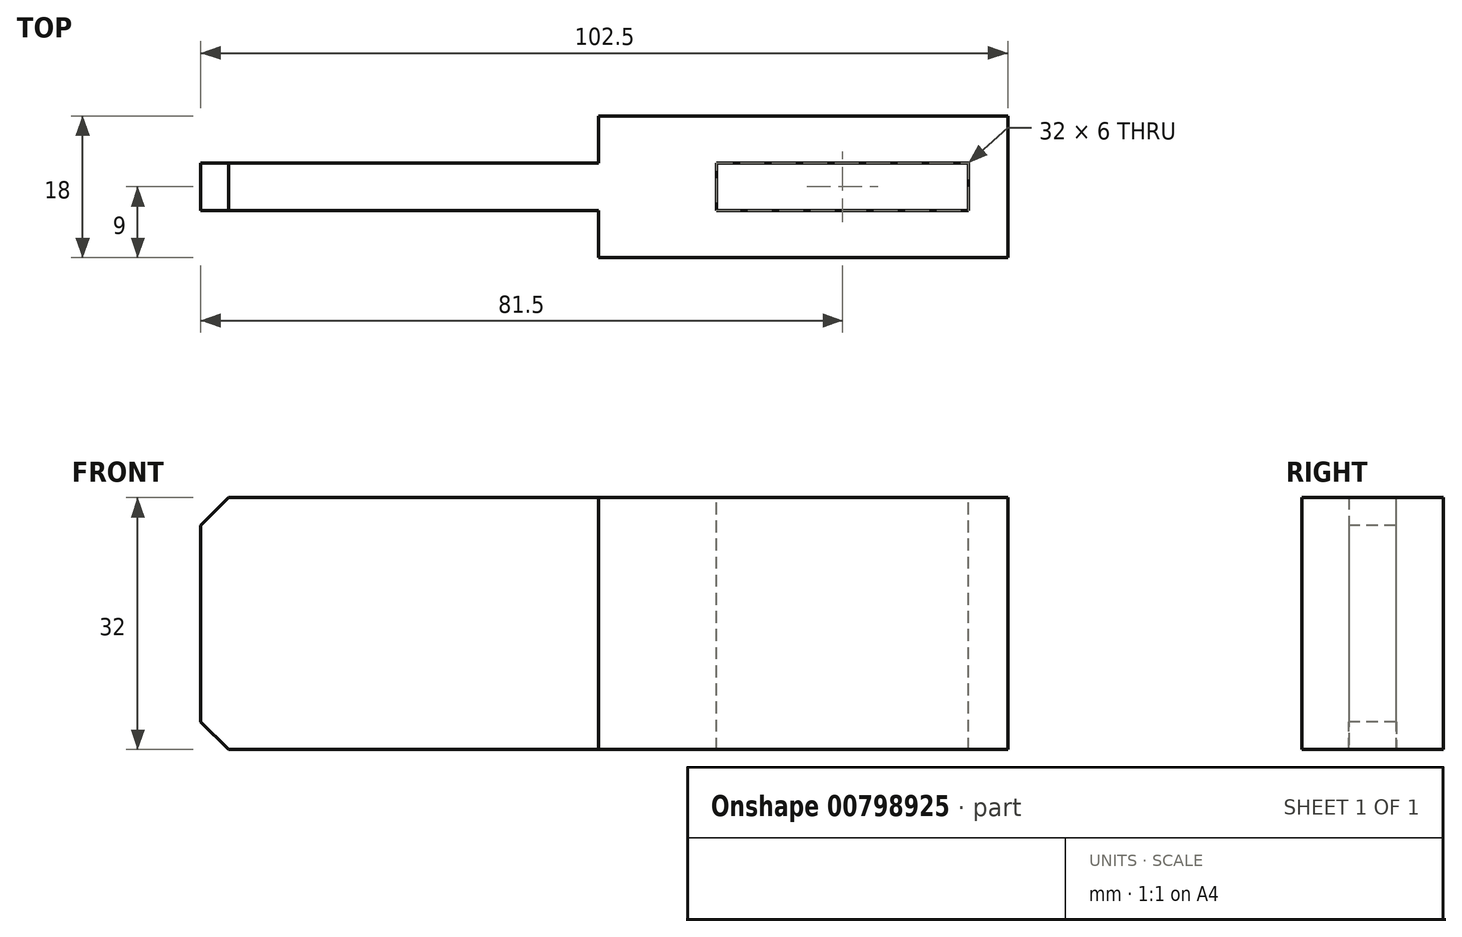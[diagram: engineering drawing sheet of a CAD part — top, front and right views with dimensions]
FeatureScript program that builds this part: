
annotation { "Feature Type Name" : "Feature", "Feature Type Description" : "" }
export const myFeature = defineFeature(function(context is Context, id is Id, definition is map)
    precondition{}
    {
        {
            var Q0;
            Q0=qCreatedBy(makeId("Front.planeOp"),FACE);
            var sketch = newSketch(context, id + "F0", { "sketchPlane" : qUnion([Q0])});
            skLineSegment(sketch, "E0", {"start": v(0, 0) * mm, "end": v(-52, 0) * mm});
            skLineSegment(sketch, "E1", {"start": v(-52, 0) * mm, "end": v(-52, 32) * mm});
            skLineSegment(sketch, "E2", {"start": v(-52, 32) * mm, "end": v(0, 32) * mm});
            skLineSegment(sketch, "E3", {"start": v(0, 32) * mm, "end": v(0, 0) * mm});
            skSolve(sketch);
        }
        {
            var Q0;
            Q0=makeQuery(id+"F0.imprint","IMPRINT",FACE,{"disambiguationData":[TD([[makeQuery(id+"F0.imprint","IMPRINT",EDGE,{"derivedFrom":sQuery(id+"F0.wireOp",EDGE,"E0")}),-1.0]])]});
            extrude(context, id + "F1", {"entities" : qUnion([Q0]), "endBound" : BoundingType.SYMMETRIC, "depth" : 18 * mm});
        }
        {
            var Q0;
            Q0=makeQuery(id+"F1.opExtrude","SWEPT_FACE",FACE,{"disambiguationData":[OSD([sQuery(id+"F0.wireOp",EDGE,"E2")])]});
            var sketch = newSketch(context, id + "F2", { "sketchPlane" : qUnion([Q0])});
            skLineSegment(sketch, "E4", {"start": v(0, 9) * mm, "end": v(0, 3) * mm});
            skLineSegment(sketch, "E5", {"start": v(0, 3) * mm, "end": v(-5, 3) * mm});
            skLineSegment(sketch, "E6", {"start": v(-5, 3) * mm, "end": v(-5, -3) * mm});
            skLineSegment(sketch, "E7", {"start": v(-5, -3) * mm, "end": v(-37, -3) * mm});
            skLineSegment(sketch, "E8", {"start": v(-37, -3) * mm, "end": v(-37, 3) * mm});
            skLineSegment(sketch, "E9", {"start": v(-37, 3) * mm, "end": v(-5, 3) * mm});
            skSolve(sketch);
        }
        {
            var Q0;
            Q0=makeQuery(id+"F2.imprint","IMPRINT",FACE,{"disambiguationData":[TD([[makeQuery(id+"F2.imprint","IMPRINT",EDGE,{"derivedFrom":sQuery(id+"F2.wireOp",EDGE,"E6")}),-1.0]])]});
            extrude(context, id + "F3", {"entities" : qUnion([Q0]), "operationType" : NewBodyOperationType.REMOVE, "endBound" : BoundingType.THROUGH_ALL, "oppositeDirection" : true, "depth" : 25 * mm});
        }
        {
            var Q0;
            Q0=makeQuery(id+"F1.opExtrude","SWEPT_FACE",FACE,{"disambiguationData":[OSD([sQuery(id+"F0.wireOp",EDGE,"E1")])]});
            var sketch = newSketch(context, id + "F4", { "sketchPlane" : qUnion([Q0])});
            skLineSegment(sketch, "E10", {"start": v(9, 32) * mm, "end": v(3, 32) * mm});
            skLineSegment(sketch, "E11", {"start": v(3, 32) * mm, "end": v(3, 0) * mm});
            skLineSegment(sketch, "E12", {"start": v(3, 0) * mm, "end": v(-3, 0) * mm});
            skLineSegment(sketch, "E13", {"start": v(-3, 0) * mm, "end": v(-3, 32) * mm});
            skLineSegment(sketch, "E14", {"start": v(-3, 32) * mm, "end": v(3, 32) * mm});
            skSolve(sketch);
        }
        {
            var Q0;
            Q0=makeQuery(id+"F4.imprint","IMPRINT",FACE,{"disambiguationData":[TD([[makeQuery(id+"F4.imprint","IMPRINT",EDGE,{"derivedFrom":sQuery(id+"F4.wireOp",EDGE,"E11")}),-1.0]])]});
            extrude(context, id + "F5", {"entities" : qUnion([Q0]), "operationType" : NewBodyOperationType.ADD, "depth" : 50.5 * mm});
        }
        {
            var Q0;
            Q0=makeQuery(id+"F5.opExtrude","SWEPT_FACE",FACE,{"disambiguationData":[OSD([sQuery(id+"F4.wireOp",EDGE,"E11")])]});
            var sketch = newSketch(context, id + "F6", { "sketchPlane" : qUnion([Q0])});
            skLineSegment(sketch, "E15", {"start": v(-52, 32) * mm, "end": v(-99, 32) * mm});
            skLineSegment(sketch, "E16", {"start": v(-99, 32) * mm, "end": v(-102.5, 28.5) * mm});
            skLineSegment(sketch, "E17", {"start": v(-52, 0) * mm, "end": v(-99, 0) * mm});
            skLineSegment(sketch, "E18", {"start": v(-99, 0) * mm, "end": v(-102.5, 3.5) * mm});
            skSolve(sketch);
        }
        {
            var Q0;
            {var subQ0=sQuery(id+"F6.wireOp",EDGE,"E16");Q0=makeQuery(id+"F6.imprint","IMPRINT",FACE,{"disambiguationData":[TD([[makeQuery(id+"F6.imprint","IMPRINT",EDGE,{"derivedFrom":subQ0}),-1.0]])]});}
            var Q1;
            {var subQ0=sQuery(id+"F6.wireOp",EDGE,"E18");Q1=makeQuery(id+"F6.imprint","IMPRINT",FACE,{"disambiguationData":[TD([[makeQuery(id+"F6.imprint","IMPRINT",EDGE,{"derivedFrom":subQ0}),1.0]])]});}
            extrude(context, id + "F7", {"entities" : qUnion([Q0, Q1]), "operationType" : NewBodyOperationType.REMOVE, "endBound" : BoundingType.THROUGH_ALL, "oppositeDirection" : true, "depth" : 25 * mm});
        }
    });
